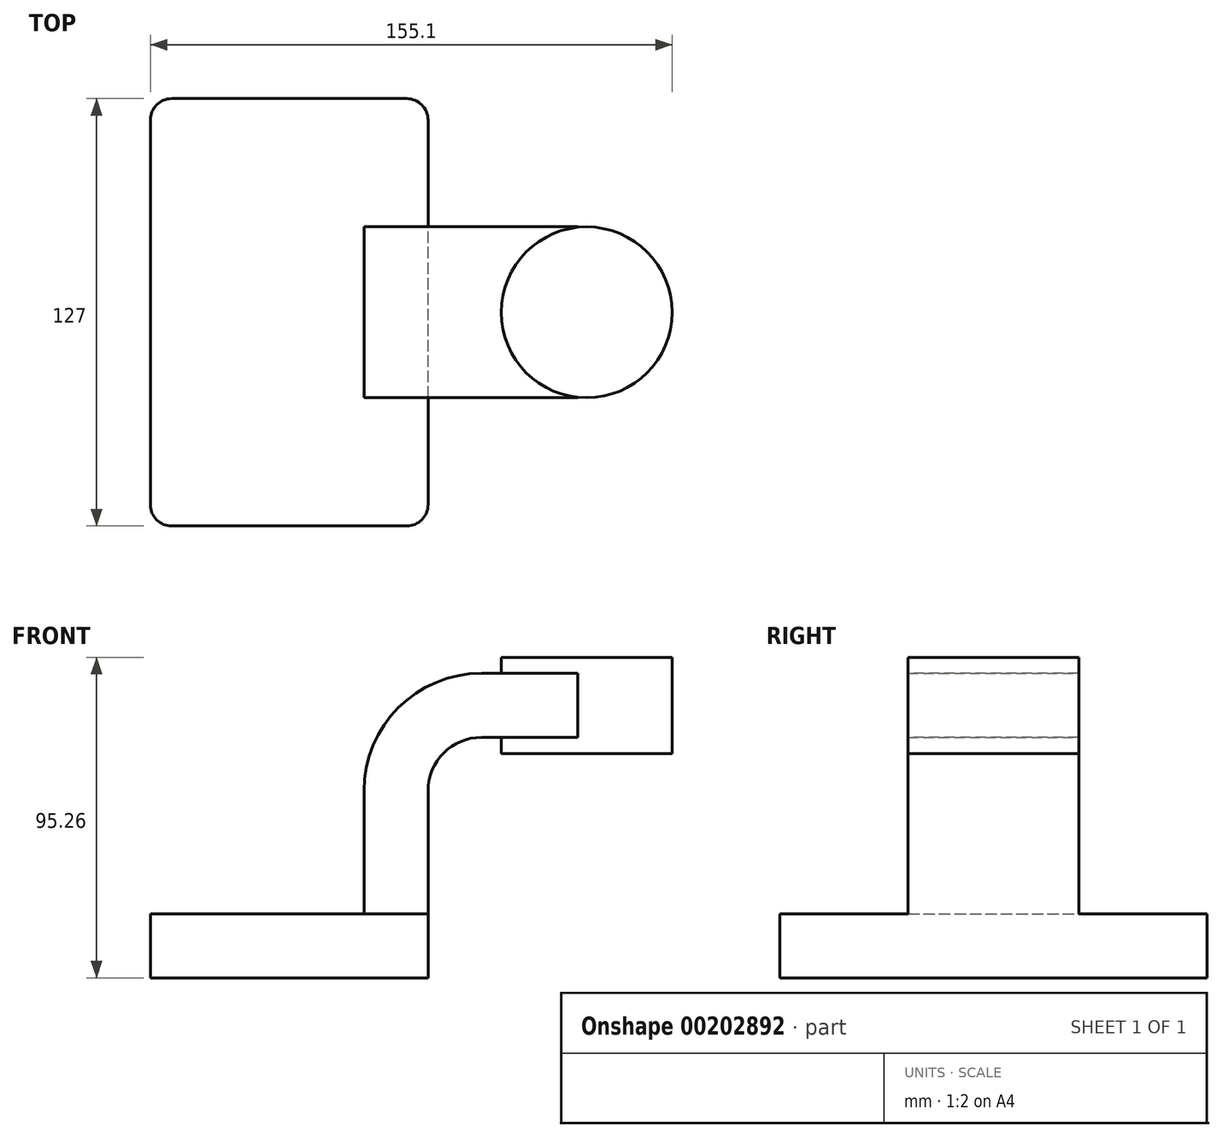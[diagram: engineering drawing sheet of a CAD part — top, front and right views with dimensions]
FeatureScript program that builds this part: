
annotation { "Feature Type Name" : "Feature", "Feature Type Description" : "" }
export const myFeature = defineFeature(function(context is Context, id is Id, definition is map)
    precondition{}
    {
        {
            var Q0;
            Q0=qCreatedBy(makeId("Front.planeOp"),FACE);
            var sketch = newSketch(context, id + "F0", { "sketchPlane" : qUnion([Q0])});
            skLineSegment(sketch, "E0.bottom", {"start": v(41.27, 9.53) * mm, "end": v(-41.28, 9.53) * mm});
            skLineSegment(sketch, "E0.top", {"start": v(41.28, -9.52) * mm, "end": v(-41.27, -9.52) * mm});
            skLineSegment(sketch, "E0.left", {"start": v(41.28, 9.53) * mm, "end": v(41.28, -9.52) * mm});
            skLineSegment(sketch, "E0.right", {"start": v(-41.28, 9.53) * mm, "end": v(-41.27, -9.52) * mm});
            skPoint(sketch, "E0.middle", {"position": v(0, 0) * mm});
            skLineSegment(sketch, "E1.bottom", {"start": v(113.83, 85.73) * mm, "end": v(63.03, 85.73) * mm});
            skLineSegment(sketch, "E1.top", {"start": v(113.83, 57.15) * mm, "end": v(63.03, 57.15) * mm});
            skLineSegment(sketch, "E1.left", {"start": v(113.83, 85.73) * mm, "end": v(113.83, 57.15) * mm});
            skLineSegment(sketch, "E1.right", {"start": v(63.03, 85.73) * mm, "end": v(63.03, 57.15) * mm});
            skPoint(sketch, "E1.middle", {"position": v(88.43, 71.44) * mm});
            skLineSegment(sketch, "E2", {"start": v(41.27, 9.53) * mm, "end": v(41.27, 46.05) * mm});
            skArc(sketch, "E3", {"start": v(41.27, 46.05) * mm, "mid": v(45.92, 57.28) * mm, "end": v(57.15, 61.93) * mm});
            skLineSegment(sketch, "E4", {"start": v(57.15, 61.93) * mm, "end": v(85.72, 61.93) * mm});
            skLineSegment(sketch, "E5.0", {"start": v(57.15, 80.98) * mm, "end": v(85.72, 80.98) * mm});
            skArc(sketch, "E5.1", {"start": v(22.22, 46.05) * mm, "mid": v(32.45, 70.75) * mm, "end": v(57.15, 80.98) * mm});
            skLineSegment(sketch, "E5.2", {"start": v(22.22, 9.53) * mm, "end": v(22.22, 46.05) * mm});
            skLineSegment(sketch, "E6", {"start": v(85.72, 61.93) * mm, "end": v(85.72, 80.98) * mm});
            skFitSpline(sketch, "E7", {"points": [v(-41.28, 9.53) * mm, v(57.15, 80.98) * mm], "startDerivative": vector(4.1, 114.09) * mm, "endDerivative": vector(188.44, -0.57) * mm});
            skLineSegment(sketch, "E8", {"start": v(88.43, 71.44) * mm, "end": v(88.43, 85.73) * mm});
            skLineSegment(sketch, "E9", {"start": v(88.43, 71.44) * mm, "end": v(88.43, 57.15) * mm});
            skSolve(sketch);
        }
        {
            var Q0;
            Q0=makeQuery(id+"F0.imprint","IMPRINT",FACE,{"disambiguationData":[TD([[makeQuery(id+"F0.imprint","IMPRINT",EDGE,{"derivedFrom":sQuery(id+"F0.wireOp",EDGE,"E0.top")}),-1.0]])]});
            extrude(context, id + "F1", {"entities" : qUnion([Q0]), "endBound" : BoundingType.SYMMETRIC, "depth" : 127 * mm});
        }
        {
            var Q0;
            {var subQ1=sQuery(id+"F0.wireOp",EDGE,"E2");Q0=makeQuery(id+"F0.imprint","IMPRINT",FACE,{"disambiguationData":[TD([[makeQuery(id+"F0.imprint","IMPRINT",EDGE,{"derivedFrom":subQ1}),1.0]])]});}
            var Q1;
            {var subQ5=sQuery(id+"F0.wireOp",EDGE,"E6");Q1=makeQuery(id+"F0.imprint","IMPRINT",FACE,{"disambiguationData":[TD([[makeQuery(id+"F0.imprint","IMPRINT",EDGE,{"derivedFrom":subQ5}),1.0]])]});}
            extrude(context, id + "F2", {"entities" : qUnion([Q0, Q1]), "operationType" : NewBodyOperationType.ADD, "endBound" : BoundingType.SYMMETRIC, "depth" : 50.8 * mm});
        }
        {
            var Q0;
            Q0=makeQuery(id+"F0.imprint","IMPRINT",FACE,{"disambiguationData":[TD([[makeQuery(id+"F0.imprint","IMPRINT",EDGE,{"derivedFrom":sQuery(id+"F0.wireOp",EDGE,"E5.1")}),1.0]])]});
            extrude(context, id + "F3", {"entities" : qUnion([Q0]), "operationType" : NewBodyOperationType.ADD, "endBound" : BoundingType.SYMMETRIC, "depth" : 15.88 * mm});
        }
        {
            var Q0;
            {var subQ1=sQuery(id+"F0.wireOp",EDGE,"E1.left");Q0=makeQuery(id+"F0.imprint","IMPRINT",FACE,{"disambiguationData":[TD([[makeQuery(id+"F0.imprint","IMPRINT",EDGE,{"derivedFrom":subQ1}),-1.0]])]});}
            var Q1;
            Q1=sQuery(id+"F0.wireOp",EDGE,"E9");
            revolve(context, id + "F4", {"operationType" : NewBodyOperationType.ADD, "entities" : qUnion([Q0]), "axis" : qUnion([Q1]), "revolveType" : RevolveType.FULL});
        }
        {
            var Q0;
            Q0=makeQuery(id+"F1.opExtrude","CAP_EDGE",EDGE,{"disambiguationData":[OSD([sQuery(id+"F0.wireOp",EDGE,"E0.right")])],"isStart":true});
            var Q1;
            Q1=makeQuery(id+"F1.opExtrude","CAP_EDGE",EDGE,{"disambiguationData":[OSD([sQuery(id+"F0.wireOp",EDGE,"E0.right")])],"isStart":false});
            var Q2;
            Q2=makeQuery(id+"F1.opExtrude","CAP_EDGE",EDGE,{"disambiguationData":[OSD([sQuery(id+"F0.wireOp",EDGE,"E0.left")])],"isStart":false});
            var Q3;
            Q3=makeQuery(id+"F1.opExtrude","CAP_EDGE",EDGE,{"disambiguationData":[OSD([sQuery(id+"F0.wireOp",EDGE,"E0.left")])],"isStart":true});
            fillet(context, id + "F5", {"entities" : qUnion([Q0, Q1, Q2, Q3]), "radius" : 6.35 * mm, "tangentPropagation" : true, "allowEdgeOverflow" : false});
        }
    });
